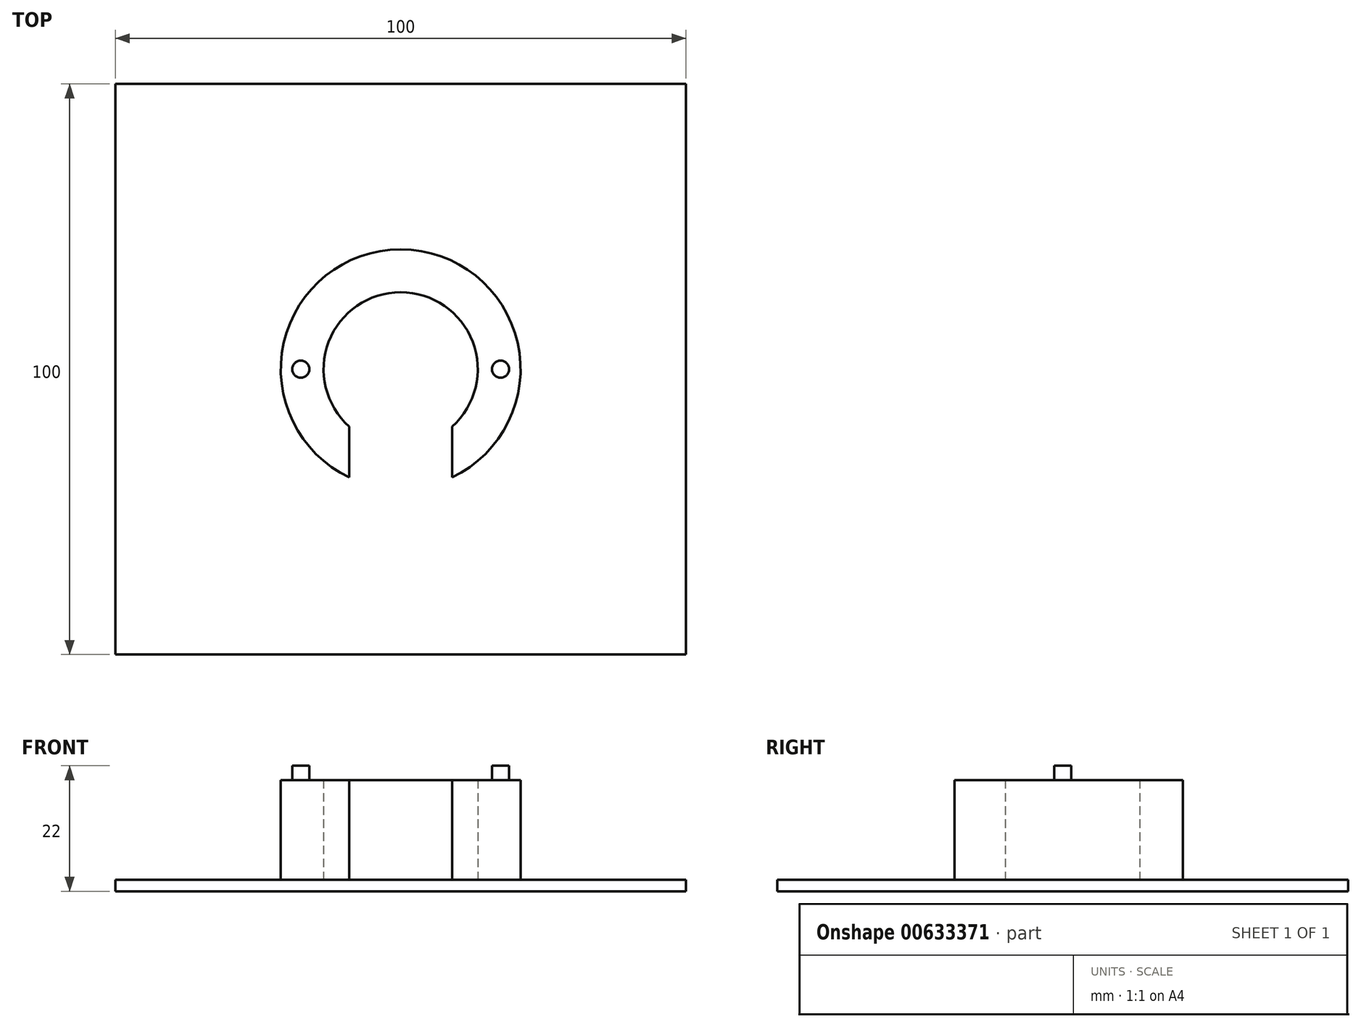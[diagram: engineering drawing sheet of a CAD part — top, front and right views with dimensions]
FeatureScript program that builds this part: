
annotation { "Feature Type Name" : "Feature", "Feature Type Description" : "" }
export const myFeature = defineFeature(function(context is Context, id is Id, definition is map)
    precondition{}
    {
        {
            var Q0;
            Q0=qCreatedBy(makeId("Top.planeOp"),FACE);
            var sketch = newSketch(context, id + "F0", { "sketchPlane" : qUnion([Q0])});
            skCircle(sketch, "E0", {"center": v(0, 0) * mm, "radius": 13.5 * mm});
            skCircle(sketch, "E1", {"center": v(0, 0) * mm, "radius": 21 * mm});
            skLineSegment(sketch, "E2.bottom", {"start": v(9, -21.47) * mm, "end": v(-9, -21.47) * mm});
            skLineSegment(sketch, "E2.top", {"start": v(9, -8.96) * mm, "end": v(-9, -8.96) * mm});
            skLineSegment(sketch, "E2.left", {"start": v(9, -21.47) * mm, "end": v(9, -8.96) * mm});
            skLineSegment(sketch, "E2.right", {"start": v(-9, -21.47) * mm, "end": v(-9, -8.96) * mm});
            skPoint(sketch, "E2.middle", {"position": v(0, -15.22) * mm});
            skLineSegment(sketch, "E3.bottom", {"start": v(50, 50) * mm, "end": v(-50, 50) * mm});
            skLineSegment(sketch, "E3.top", {"start": v(50, -50) * mm, "end": v(-50, -50) * mm});
            skLineSegment(sketch, "E3.left", {"start": v(50, 50) * mm, "end": v(50, -50) * mm});
            skLineSegment(sketch, "E3.right", {"start": v(-50, 50) * mm, "end": v(-50, -50) * mm});
            skCircle(sketch, "E4", {"center": v(-17.5, 0) * mm, "radius": 1.5 * mm});
            skCircle(sketch, "E5", {"center": v(17.5, 0) * mm, "radius": 1.5 * mm});
            skSolve(sketch);
        }
        {
            var Q0;
            Q0=makeQuery(id+"F0.imprint","IMPRINT",FACE,{"disambiguationData":[TD([[makeQuery(id+"F0.imprint","IMPRINT",EDGE,{"derivedFrom":sQuery(id+"F0.wireOp",EDGE,"E4")}),-1.0]])]});
            extrude(context, id + "F1", {"entities" : qUnion([Q0]), "depth" : 17.5 * mm, "offsetDistance" : 25 * mm});
        }
        {
            var Q0;
            Q0=makeQuery(id+"F0.imprint","IMPRINT",FACE,{"disambiguationData":[TD([[makeQuery(id+"F0.imprint","IMPRINT",EDGE,{"derivedFrom":sQuery(id+"F0.wireOp",EDGE,"E4")}),1.0]])]});
            var Q1;
            Q1=makeQuery(id+"F0.imprint","IMPRINT",FACE,{"disambiguationData":[TD([[makeQuery(id+"F0.imprint","IMPRINT",EDGE,{"derivedFrom":sQuery(id+"F0.wireOp",EDGE,"E5")}),1.0]])]});
            extrude(context, id + "F2", {"entities" : qUnion([Q0, Q1]), "operationType" : NewBodyOperationType.ADD, "depth" : 20 * mm, "offsetDistance" : 25 * mm});
        }
        {
            var Q0;
            Q0 = qSketchRegion(id + "F0", true);
            var Q1;
            Q1=makeQuery(id+"F0.imprint","IMPRINT",FACE,{"disambiguationData":[TD([[makeQuery(id+"F0.imprint","IMPRINT",EDGE,{"derivedFrom":sQuery(id+"F0.wireOp",EDGE,"E4")}),-1.0]])]});
            var Q2;
            Q2=makeQuery(id+"F0.imprint","IMPRINT",FACE,{"disambiguationData":[TD([[makeQuery(id+"F0.imprint","IMPRINT",EDGE,{"derivedFrom":sQuery(id+"F0.wireOp",EDGE,"E4")}),1.0]])]});
            var Q3;
            Q3=makeQuery(id+"F0.imprint","IMPRINT",FACE,{"disambiguationData":[TD([[makeQuery(id+"F0.imprint","IMPRINT",EDGE,{"derivedFrom":sQuery(id+"F0.wireOp",EDGE,"E5")}),1.0]])]});
            var Q4;
            {var subQ0=sQuery(id+"F0.wireOp",EDGE,"E2.left");var subQ1=sQuery(id+"F0.wireOp",EDGE,"E0");var subQ2=makeQuery(id+"F0.imprint","INTERSECT",VERTEX,{"derivedFrom":[subQ1,subQ0]});Q4=makeQuery(id+"F0.imprint","IMPRINT",FACE,{"disambiguationData":[TD([[makeQuery(id+"F0.imprint","IMPRINT",EDGE,{"disambiguationData":[TD([[subQ2,1.0]])],"derivedFrom":subQ1}),-1.0]])]});}
            var Q5;
            {var subQ5=sQuery(id+"F0.wireOp",EDGE,"E2.bottom");Q5=makeQuery(id+"F0.imprint","IMPRINT",FACE,{"disambiguationData":[TD([[makeQuery(id+"F0.imprint","IMPRINT",EDGE,{"derivedFrom":subQ5}),-1.0]])]});}
            var Q6;
            {var subQ5=sQuery(id+"F0.wireOp",EDGE,"E2.top");Q6=makeQuery(id+"F0.imprint","IMPRINT",FACE,{"disambiguationData":[TD([[makeQuery(id+"F0.imprint","IMPRINT",EDGE,{"derivedFrom":subQ5}),-1.0]])]});}
            var Q7;
            {var subQ5=sQuery(id+"F0.wireOp",EDGE,"E2.top");Q7=makeQuery(id+"F0.imprint","IMPRINT",FACE,{"disambiguationData":[TD([[makeQuery(id+"F0.imprint","IMPRINT",EDGE,{"derivedFrom":subQ5}),1.0]])]});}
            extrude(context, id + "F3", {"entities" : qUnion([Q0, Q1, Q2, Q3, Q4, Q5, Q6, Q7]), "oppositeDirection" : true, "depth" : 2 * mm, "offsetDistance" : 25 * mm});
        }
    });
